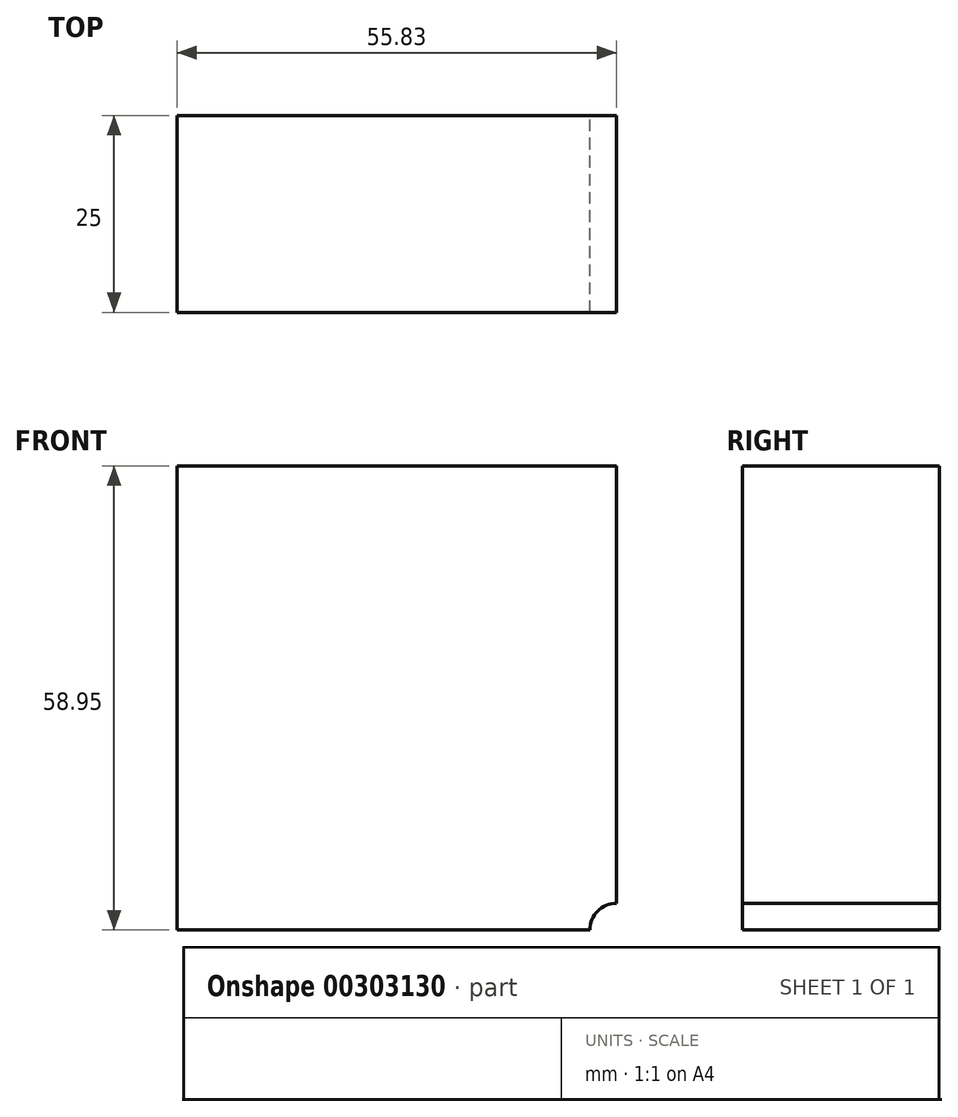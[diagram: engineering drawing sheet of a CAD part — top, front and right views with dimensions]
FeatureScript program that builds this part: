
annotation { "Feature Type Name" : "Feature", "Feature Type Description" : "" }
export const myFeature = defineFeature(function(context is Context, id is Id, definition is map)
    precondition{}
    {
        {
            var Q0;
            Q0=qCreatedBy(makeId("Front.planeOp"),FACE);
            var sketch = newSketch(context, id + "F0", { "sketchPlane" : qUnion([Q0])});
            skLineSegment(sketch, "E0.bottom", {"start": v(-97.37, 2.73) * mm, "end": v(-41.54, 2.73) * mm});
            skLineSegment(sketch, "E0.top", {"start": v(-97.37, 61.68) * mm, "end": v(-41.54, 61.68) * mm});
            skLineSegment(sketch, "E0.left", {"start": v(-97.37, 2.73) * mm, "end": v(-97.37, 61.68) * mm});
            skLineSegment(sketch, "E0.right", {"start": v(-41.54, 2.73) * mm, "end": v(-41.54, 61.68) * mm});
            skPoint(sketch, "E0.middle", {"position": v(-69.46, 32.2) * mm});
            skSolve(sketch);
        }
        {
            var Q0;
            Q0=makeQuery(id+"F0.imprint","IMPRINT",FACE,{"disambiguationData":[TD([[makeQuery(id+"F0.imprint","IMPRINT",EDGE,{"derivedFrom":sQuery(id+"F0.wireOp",EDGE,"E0.bottom")}),1.0]])]});
            extrude(context, id + "F1", {"entities" : qUnion([Q0]), "depth" : 25 * mm});
        }
        {
            var Q0;
            Q0=sQuery(id+"F0.wireOp",VERTEX,"E0.right.start");
            var Q1;
            Q1=makeQuery(id+"F1.opExtrude","SWEPT_BODY",BODY,{"disambiguationData":[OSD([sQuery(id+"F0.wireOp",EDGE,"E0.bottom"),sQuery(id+"F0.wireOp",EDGE,"E0.top"),sQuery(id+"F0.wireOp",EDGE,"E0.left"),sQuery(id+"F0.wireOp",EDGE,"E0.right")])]});
            hole(context, id + "F2", {"style" : HoleStyle.SIMPLE, "endStyle" : HoleEndStyle.THROUGH, "oppositeDirection" : true, "standardTappedOrClearance" : lookupTablePath({ "standard" : "ANSI", "fit" : "Normal (ASME)", "size" : "1/4", "type" : "Clearance" }), "standardBlindInLast" : lookupTablePath({ "fit" : "Free", "standard" : "ANSI", "size" : "1/4", "type" : "Clearance" }), "holeDiameter" : 6.76 * mm, "tappedDepth" : 12 * mm, "tapClearance" : 3, "locations" : qUnion([Q0]), "scope" : qUnion([Q1])});
        }
    });
